# Revit family: PRD_AR_WtrSpplFttngsFrWshBsnsAndTrghs_ElectronicTapMixer_F5ET1010-1015
name_source: partatom
category: Plumbing Fixtures
revit_build: Autodesk Revit 2018 (Build: 20190510_1515(x64)
units: mm (PartAtom-declared; Revit-internal decimal feet)

## family parameters
Cut with Voids When Loaded = Yes
Host = Face
OmniClass Number = 23.45.55.17
OmniClass Title = Mixing Faucets
Part Type = Normal
Room Calculation Point = No
Round Connector Dimension = Use Diameter
Shared = No

## types (3) — shared parameters
AssetType = Fixed
CasingMaterial = PRD_AR_StainlessSteel_SatinFinished
Category = Pr_40_20_87_98, Washbasin taps
Color = satin finished
Default Elevation = 850 mm  [stored 2.78871 ft]
DefaultAutomaticHygieneFlushing = 24h after the last activity
Depressurised = no
DiameterNominal = 15  [stored 0.0492126 ft]
DurationUnit = year
FaucetFunction = MIXED
FaucetMaterial = PRD_AR_ChromatedBrass_HighPolished
FaucetOperation = SELFCLOSING
FaucetType = SINGLEOUTLETCOMBINATION
Features = For sanitary facilities, for connection to hot water and cold water, stainless steel cover plate 190 x 245 mm.
Finish = high-polished chromium-plated brass
FlowColdWater = 0.1 L/s
FlowHotWater = 0.1 L/s
FunctionalPrinciple = electronic self-closing
HygieneFlushing = yes
IfcExportAs = IfcValveType
IfcExportType = FAUCET
InletSize = G-3-4-B
Manufacturer = KWC Group AG
ManufacturerName = KWC Group AG
ManufacturerURL = www.kwc.com
Material = stainless steel
MaterialsBody = Brass
MinimumFlowPressure = 1.00 bar
NBSDescription = Water supply fittings for wash basins and troughs
NBSReference = 45-35-70/371
NominalHeight = 245 mm  [stored 0.803806 ft]
NominalWidth = 190 mm
OutletMaterial = PRD_AR_SyntheticGrey
PositionOfPowerConnection = from top
PowerConsumption = 1.5
PowerSupplyConnection = 6,75 / 12 V DC / A3000 open
ProductInformation = https://pim.kwc.com
ProtectiveShutdown = yes
ProtectiveSystemIP = IP59K
SensorMaterial = PRD_AR_SyntheticBlack
SoundInsulation = no
ThermalDisinfection = prepared for automatic thermal disinfection
TypeOfMixing = with thermostat
TypeOfMounting = in-wall installation with box
TypeOfOperation = sensor operation
TypeOfSensor = opto-electronic sensor
TypeOfTap = in-wall tap
URL = www.kwc.com
Uniclass2015Code = Pr_40_20_87_98
Uniclass2015Title = Washbasin taps
Uniclass2015Version = Products v1.10
Version = 1
VolumeFlowRate = 0.10 L/s at 3 bar
VolumeFlowRateBypass = 0.05 liter per second
WarrantyDurationUnit = year
zero-valued in all types: NominalLength

## per-type parameters (varying)
| type | BIMObjectName | Description | GrossWeight | LengthToSpout | Model | ModelNumber | ModelReference | Name | NetWeight | SpoutProjection |
| F5ET1013 - 0.10 L/s with separate power supply via power supply unit 6.75 V / 12 V DC, projection 140 mm | PRD_AR_WaterSupplyFittingsForWashBasinsAndTroughs_ElectronicThermostaticMixer_F5ET1013 | F5E-Therm thermostatic mixer DN 15 as finished installation kit for in-wall installation in basic installation kit, for sanitary facilities. Opto-electronically controlled, for connection to hot water and cold water. Function block with integrated solenoid valve cartridge, thermostat and device for optional bypass solenoid valve cartridge, for program-controlled thermal disinfection. Thermostat with metal handle with adjustable and turn-proof temperature stop and option for manual thermal disinfection. Visible parts made of high-polished chromium-plated brass. Holding frame with profile seal, stainless steel cover plate 190 x 245 mm with covered screw fixing including sensor with control electronics, rosette, backflow preventer and strainers. Spout with laminar jet controller with integrated flow regulator 6.0 l/min. Projection 140 mm, depth adjustability 25 mm. Activated water hygiene flushing 24 hours after last activation, safety switch-off with continuous reflection and saving of statistical data. With option for parameterization and communication via optional, bidirectional remote control. Separate power supply via power supply unit 6.75 V / 12 V DC or AQUA 3000 open system accessories. | 4.53 kg | 140 mm  [stored 0.459318 ft] | F5ET1013 | 2030038681 | F5ET1013 | F5 electronic thermostatic mixer F5ET1013 | 4.26 kg | 140.00 mm |
| F5ET1014 - 0.10 L/s with separate power supply via power supply unit 6.75 V / 12 V DC, projection 200 mm | PRD_AR_WaterSupplyFittingsForWashBasinsAndTroughs_ElectronicThermostaticMixer_F5ET1014 | F5E-Therm thermostatic mixer DN 15 as finished installation kit for in-wall installation in basic installation kit, for sanitary facilities. Opto-electronically controlled, for connection to hot water and cold water. Function block with integrated solenoid valve cartridge, thermostat and device for optional bypass solenoid valve cartridge, for program-controlled thermal disinfection. Thermostat with metal handle with adjustable and turn-proof temperature stop and option for manual thermal disinfection. Visible parts made of high-polished chromium-plated brass. Holding frame with profile seal, stainless steel cover plate 190 x 245 mm with covered screw fixing including sensor with control electronics, rosette, backflow preventer and strainers. Spout with laminar jet controller with integrated flow regulator 6.0 l/min. Projection 200 mm, depth adjustability 25 mm. Activated water hygiene flushing 24 hours after last activation, safety switch-off with continuous reflection and saving of statistical data. With option for parameterization and communication via optional, bidirectional remote control. Separate power supply via power supply unit 6.75 V / 12 V DC or AQUA 3000 open system accessories. | 4.57 kg | 200 mm  [stored 0.656168 ft] | F5ET1014 | 2030038682 | F5ET1014 | F5 electronic thermostatic mixer F5ET1014 | 4.34 kg | 200.00 mm |
| F5ET1015 - 0.10 L/s with separate power supply via power supply unit 6.75 V / 12 V DC, projection 260 mm | PRD_AR_WaterSupplyFittingsForWashBasinsAndTroughs_ElectronicThermostaticMixer_F5ET1015 | F5E-Therm thermostatic mixer DN 15 as finished installation kit for in-wall installation in basic installation kit, for sanitary facilities. Opto-electronically controlled, for connection to hot water and cold water. Function block with integrated solenoid valve cartridge, thermostat and device for optional bypass solenoid valve cartridge, for program-controlled thermal disinfection. Thermostat with metal handle with adjustable and turn-proof temperature stop and option for manual thermal disinfection. Visible parts made of high-polished chromium-plated brass. Holding frame with profile seal, stainless steel cover plate 190 x 245 mm with covered screw fixing including sensor with control electronics, rosette, backflow preventer and strainers. Spout with laminar jet controller with integrated flow regulator 6.0 l/min. Projection 260 mm, depth adjustability 25 mm. Activated water hygiene flushing 24 hours after last activation, safety switch-off with continuous reflection and saving of statistical data. With option for parameterization and communication via optional, bidirectional remote control. Separate power supply via power supply unit 6.75 V / 12 V DC or AQUA 3000 open system accessories. | 5.20 kg | 260 mm  [stored 0.853018 ft] | F5ET1015 | 2030038683 | F5ET1015 | F5 electronic thermostatic mixer F5ET1015 | 5.00 kg | 260.00 mm |

note: [stored X ft] marks values corroborated as IEEE doubles in the binary element streams (Revit-internal decimal feet)

## geometry (parser evidence)
native form markers: Sweep x6
no freeform markers — native parametric forms only
